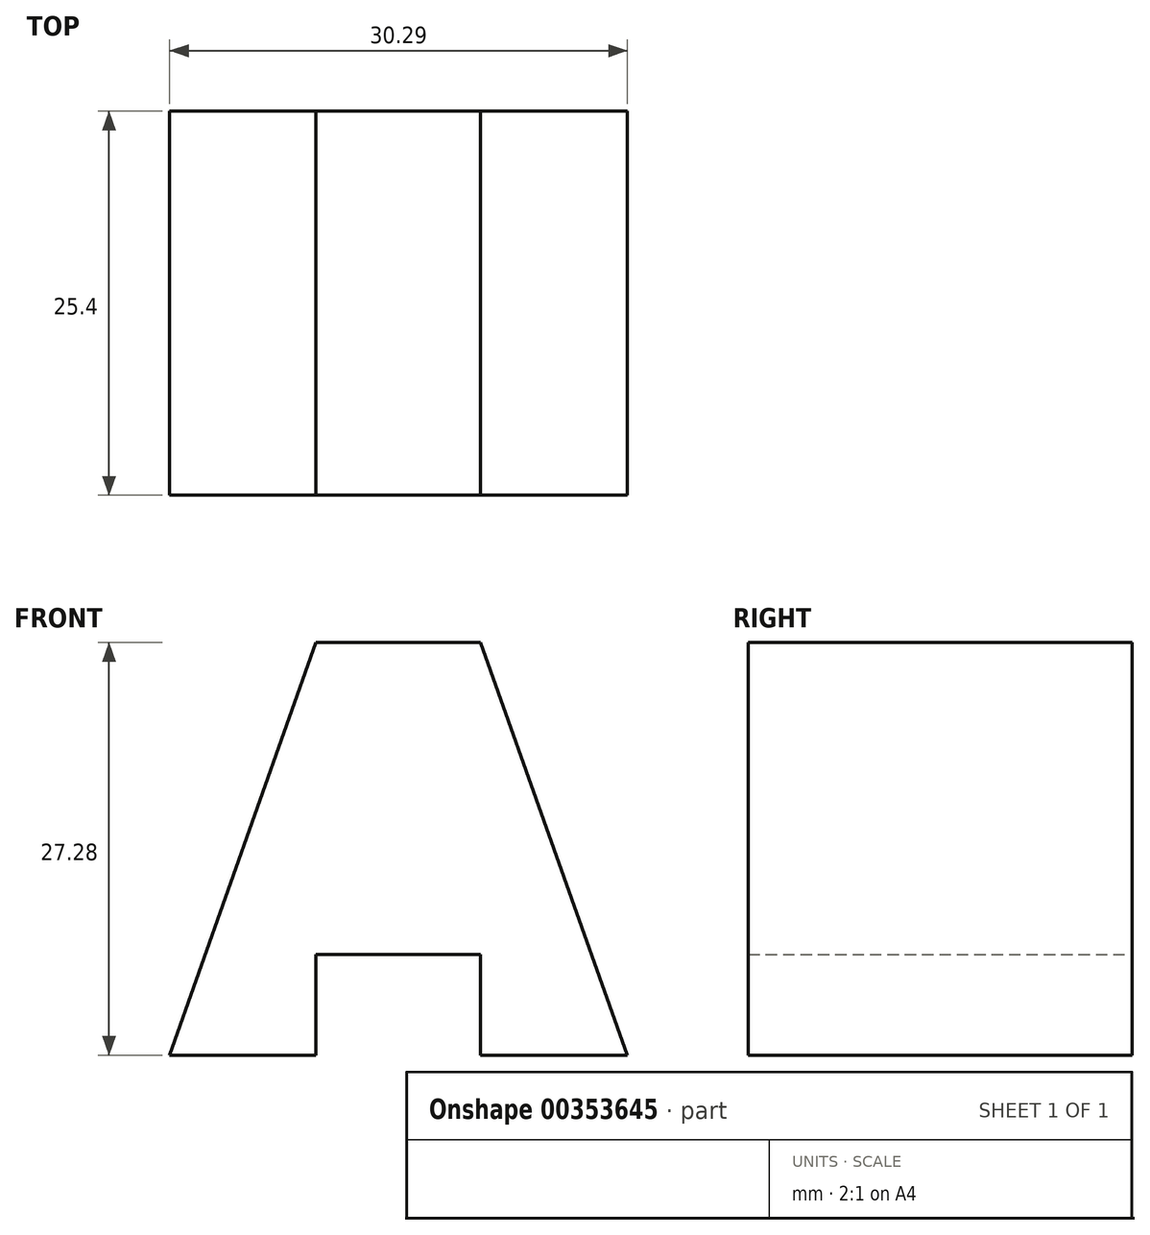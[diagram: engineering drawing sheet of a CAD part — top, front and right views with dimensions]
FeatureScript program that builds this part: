
annotation { "Feature Type Name" : "Feature", "Feature Type Description" : "" }
export const myFeature = defineFeature(function(context is Context, id is Id, definition is map)
    precondition{}
    {
        {
            var Q0;
            Q0=qCreatedBy(makeId("Front.planeOp"),FACE);
            var sketch = newSketch(context, id + "F0", { "sketchPlane" : qUnion([Q0])});
            skLineSegment(sketch, "E0", {"start": v(-56.39, 0) * mm, "end": v(-46.73, 27.28) * mm});
            skLineSegment(sketch, "E1", {"start": v(-46.73, 27.28) * mm, "end": v(-35.82, 27.28) * mm});
            skLineSegment(sketch, "E2", {"start": v(-35.82, 27.28) * mm, "end": v(-26.1, 0) * mm});
            skLineSegment(sketch, "E3", {"start": v(-56.39, 0) * mm, "end": v(-46.73, 0) * mm});
            skLineSegment(sketch, "E4", {"start": v(-26.1, 0) * mm, "end": v(-35.82, 0) * mm});
            skLineSegment(sketch, "E5", {"start": v(-46.73, 0) * mm, "end": v(-46.73, 6.66) * mm});
            skLineSegment(sketch, "E6", {"start": v(-46.73, 6.66) * mm, "end": v(-35.82, 6.66) * mm});
            skLineSegment(sketch, "E7", {"start": v(-35.82, 6.66) * mm, "end": v(-35.82, 0) * mm});
            skSolve(sketch);
        }
        {
            var Q0;
            Q0=makeQuery(id+"F0.imprint","IMPRINT",FACE,{"disambiguationData":[TD([[makeQuery(id+"F0.imprint","IMPRINT",EDGE,{"derivedFrom":sQuery(id+"F0.wireOp",EDGE,"E0")}),-1.0]])]});
            extrude(context, id + "F1", {"entities" : qUnion([Q0]), "depth" : 25.4 * mm});
        }
    });
